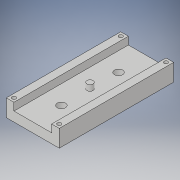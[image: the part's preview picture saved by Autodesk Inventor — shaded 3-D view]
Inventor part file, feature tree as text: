
AUTODESK INVENTOR PART (.ipt)
format: ipt  version: 2019 (Build 230136000, 136)  size: 159,232 bytes
history: native  units: mm
features: sketch x5, extrude x4, hole x1
ambient origin geometry x8: Origin, YZ Plane, XZ Plane, XY Plane, X Axis, Y Axis, Z Axis, Center Point
bodies: Solid1 (feature_tree)
feature tree (10):
  extrude  "Extrusion1"  Depth=27.747mm
  extrude  "Extrusion2"  Depth=4.0mm
  extrude  "Extrusion3"  Depth=4.0mm TaperAngle=0.0deg
  hole  "Hole1"  [1 undecoded]
  extrude  "Extrusion4"  Depth=2.0mm
  sketch  "Sketch1"  dims[d0=60.0mm d1=27.747mm]
  sketch  "Sketch2"  dims[d2=5.0mm d3=0.0mm d4=4.0mm]
  sketch  "Sketch3"  dims[d5=4.0mm d6=4.0mm d7=0.0mm]
  sketch  "Sketch4"  dims[d8=3.175mm d9=3.0mm d10=0.0mm]
  sketch  "Sketch5"  dims[d11=4.305mm d12=6.0mm d13=7.087mm d14=2.0mm d15=14.3117mm d16=8.0mm d17=20.594885mm d18=2.0mm d19=2.0mm d20=2.0mm d21=3.0mm d22=0.0mm]
note: 1 required parameter value undecoded (feature->parameter linkage not recoverable at this tier; creation-order binding heuristic only, values carry confidence <= 0.55)
